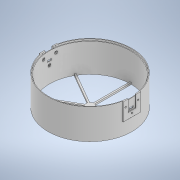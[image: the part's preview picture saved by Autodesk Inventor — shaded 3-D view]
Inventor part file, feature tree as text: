
AUTODESK INVENTOR PART (.ipt)
format: ipt  version: 2020.2 (Build 242310000, 310)  size: 463,872 bytes
history: native  units: mm
features: extrude x10, sketch x10, plane x2, pattern_circular x1
ambient origin geometry x8: Origin, YZ Plane, XZ Plane, XY Plane, X Axis, Y Axis, Z Axis, Center Point
bodies: Solid1 (feature_tree)
feature tree (23):
  extrude  "Extrusion1"  Depth=2.0mm
  extrude  "Extrusion2"  TaperAngle=360.0deg  [1 undecoded]
  plane  "Work Plane2"
  extrude  "Extrusion8"  Depth=215.0mm
  extrude  "Extrusion4"  Depth=73.5mm TaperAngle=0.0deg
  extrude  "Extrusion6"  TaperAngle=0.0deg  [1 undecoded]
  plane  "Work Plane4"
  extrude  "Extrusion9"  Depth=10.0mm
  extrude  "Extrusion10"  Depth=2.0mm
  extrude  "Extrusion11"  Depth=4.0mm TaperAngle=0.0deg
  pattern_circular  "Circular Pattern2"  [2 undecoded]
  extrude  "Extrusion12"  Depth=2.0mm TaperAngle=0.0deg
  extrude  "Extrusion13"  TaperAngle=0.0deg  [1 undecoded]
  sketch  "Sketch2"  dims[d15=2.0mm d34=10.081707mm]
  sketch  "Sketch3"  dims[d35=60.0mm d37=360.0deg]
  sketch  "Sketch5"  dims[d41=4.0mm d42=0.0mm d43=215.0mm]
  sketch  "Sketch7"  dims[d44=205.0mm d45=73.5mm d46=0.0mm]
  sketch  "Sketch9"  dims[d60=20.0mm d61=0.0mm]
  sketch  "Sketch10"  dims[d62=30.0mm d63=10.0mm]
  sketch  "Sketch11"  dims[d64=2.0mm d65=0.0mm d84=208.233333mm]
  sketch  "Sketch12"  dims[d85=211.766667mm d86=4.0mm d87=0.0mm]
  sketch  "Sketch13"  dims[d88=-5.0mm]
  sketch  "Sketch14"  dims[d101=3.0mm d102=0.0mm d103=4.0mm d104=0.0mm d107=2.0mm d108=0.0mm d109=0.0mm d110=45.0mm d111=22.5mm d112=45.0mm d122=3.0mm d123=20.0mm d124=30.0mm d126=5.0mm d127=10.0mm d128=4.0mm d129=4.0mm d130=6.0mm d131=15.0mm d132=4.0mm d133=6.0mm d134=10.0mm d135=15.0mm d136=0.0mm d141=0.0mm d142=20.0mm d143=2.0mm d144=0.0mm d145=6.0mm d146=15.0mm d147=7.0mm d148=7.0mm d149=6.0mm d150=10.0mm d151=0.0mm d152=0.0mm d153=3.0mm d154=5.0mm d155=0.0mm d156=0.0mm d157=20.0mm d158=360.0deg d160=10.0mm d161=0.0mm d162=60.0mm d164=360.0deg d166=69.5mm d167=0.0mm d39=0.5mm d40=0.872665mm]
note: 5 required parameter values undecoded (feature->parameter linkage not recoverable at this tier; creation-order binding heuristic only, values carry confidence <= 0.55)
